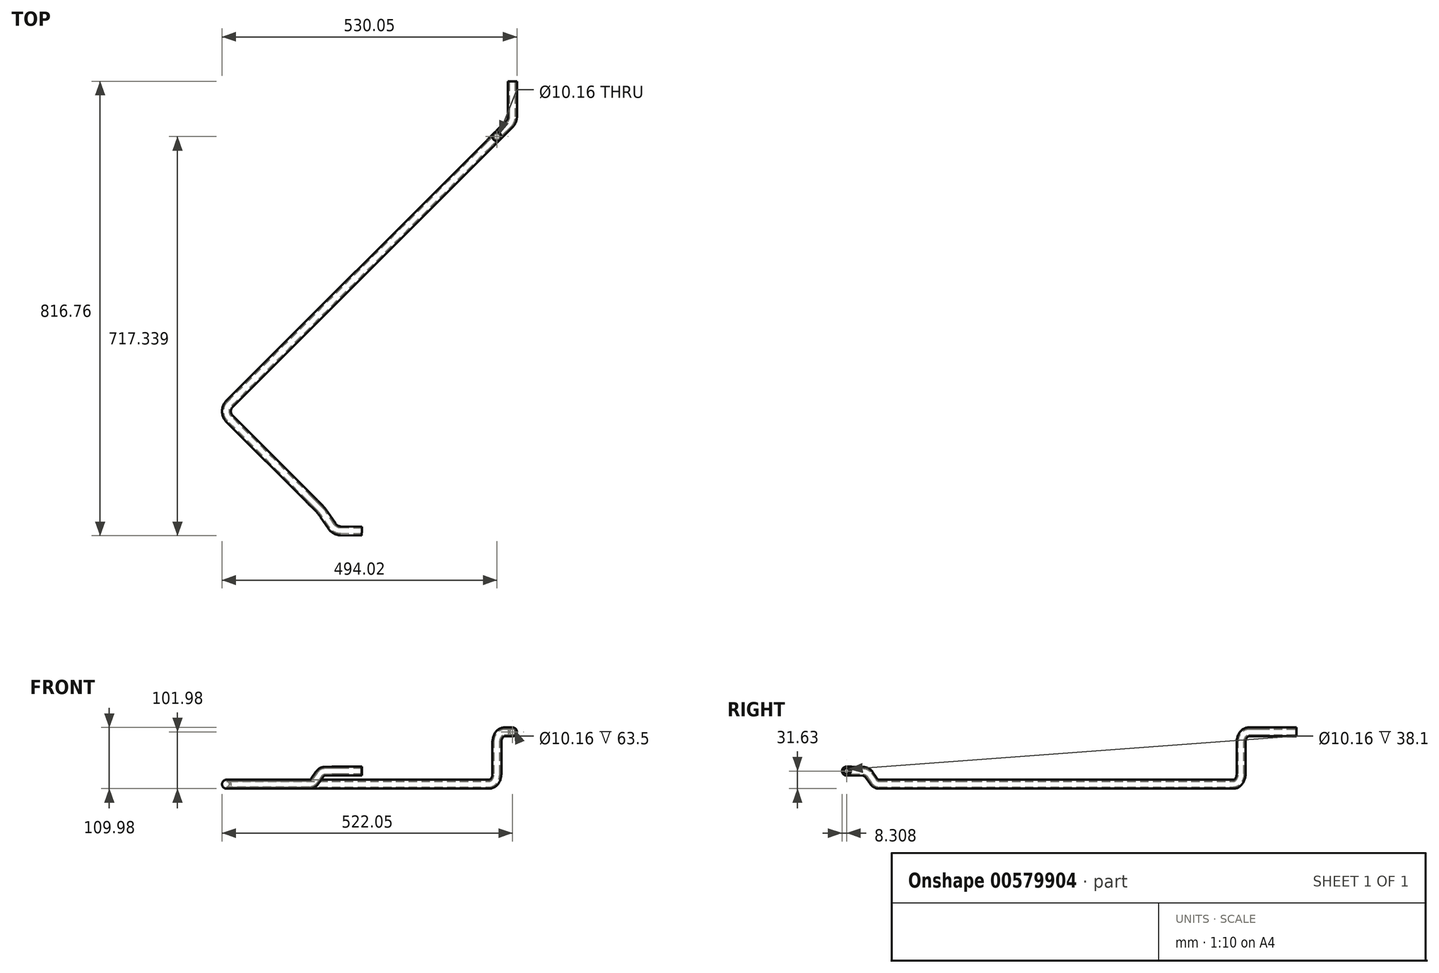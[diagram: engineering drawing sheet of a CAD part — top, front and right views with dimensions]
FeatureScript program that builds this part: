
annotation { "Feature Type Name" : "Feature", "Feature Type Description" : "" }
export const myFeature = defineFeature(function(context is Context, id is Id, definition is map)
    precondition{}
    {
        {
            var Q0;
            Q0=qCreatedBy(makeId("Front.planeOp"),FACE);
            var sketch = newSketch(context, id + "F0", { "sketchPlane" : qUnion([Q0])});
            skCircle(sketch, "E0", {"center": v(0, 0) * mm, "radius": 8 * mm});
            skCircle(sketch, "E1", {"center": v(0, 0) * mm, "radius": 5.08 * mm});
            skSolve(sketch);
        }
        {
            var Q0;
            Q0=qSketchRegion(id+"F0",true);
            extrude(context, id + "F1", {"entities" : qUnion([Q0]), "depth" : 63.5 * mm, "offsetDistance" : 25.4 * mm});
        }
        {
            var Q0;
            Q0=makeQuery(id+"F1.opExtrude","CAP_FACE",FACE,{"disambiguationData":[OSD([sQuery(id+"F0.wireOp",EDGE,"E0"),sQuery(id+"F0.wireOp",EDGE,"E1")])],"isStart":false});
            var sketch = newSketch(context, id + "F2", { "sketchPlane" : qUnion([Q0])});
            skCircle(sketch, "E2", {"center": v(0, 0) * mm, "radius": 5.08 * mm});
            skCircle(sketch, "E3", {"center": v(0, 0) * mm, "radius": 8 * mm});
            skLineSegment(sketch, "E4", {"start": v(-19.05, 9.37) * mm, "end": v(-19.05, -12.33) * mm});
            skSolve(sketch);
        }
        {
            var Q0;
            Q0 = qSketchRegion(id + "F2", true);
            var Q1;
            Q1=sQuery(id+"F2.wireOp",EDGE,"E4");
            revolve(context, id + "F3", {"operationType" : NewBodyOperationType.ADD, "entities" : qUnion([Q0]), "axis" : qUnion([Q1]), "revolveType" : RevolveType.ONE_DIRECTION, "angle" : 45 * degree});
        }
        {
            var Q0;
            Q0=makeQuery(id+"F3.opRevolve","CAP_FACE",FACE,{"disambiguationData":[OSD([sQuery(id+"F2.wireOp",EDGE,"E2"),sQuery(id+"F2.wireOp",EDGE,"E3")])],"isStart":false});
            var sketch = newSketch(context, id + "F4", { "sketchPlane" : qUnion([Q0])});
            skCircle(sketch, "E5", {"center": v(50.48, 0) * mm, "radius": 5.08 * mm});
            skCircle(sketch, "E6", {"center": v(50.48, 0) * mm, "radius": 8 * mm});
            skSolve(sketch);
        }
        {
            var Q0;
            Q0 = qSketchRegion(id + "F4", true);
            extrude(context, id + "F5", {"entities" : qUnion([Q0]), "operationType" : NewBodyOperationType.ADD, "depth" : 12.7 * mm, "offsetDistance" : 25.4 * mm});
        }
        {
            var Q0;
            Q0=makeQuery(id+"F5.opExtrude","CAP_FACE",FACE,{"disambiguationData":[OSD([sQuery(id+"F4.wireOp",EDGE,"E5"),sQuery(id+"F4.wireOp",EDGE,"E6")])],"isStart":false});
            var sketch = newSketch(context, id + "F6", { "sketchPlane" : qUnion([Q0])});
            skCircle(sketch, "E7", {"center": v(50.48, 0) * mm, "radius": 5.08 * mm});
            skCircle(sketch, "E8", {"center": v(50.48, 0) * mm, "radius": 8 * mm});
            skLineSegment(sketch, "E9", {"start": v(33.2, -19.05) * mm, "end": v(65.64, -19.05) * mm});
            skSolve(sketch);
        }
        {
            var Q0;
            Q0 = qSketchRegion(id + "F6", true);
            var Q1;
            Q1=sQuery(id+"F6.wireOp",EDGE,"E9");
            revolve(context, id + "F7", {"operationType" : NewBodyOperationType.ADD, "entities" : qUnion([Q0]), "axis" : qUnion([Q1]), "revolveType" : RevolveType.ONE_DIRECTION, "angle" : 90 * degree});
        }
        {
            var Q0;
            Q0=makeQuery(id+"F7.opRevolve","CAP_FACE",FACE,{"disambiguationData":[OSD([sQuery(id+"F6.wireOp",EDGE,"E7"),sQuery(id+"F6.wireOp",EDGE,"E8")])],"isStart":false});
            var sketch = newSketch(context, id + "F8", { "sketchPlane" : qUnion([Q0])});
            skCircle(sketch, "E10", {"center": v(-28.03, 99.42) * mm, "radius": 5.08 * mm});
            skCircle(sketch, "E11", {"center": v(-28.03, 99.42) * mm, "radius": 8 * mm});
            skSolve(sketch);
        }
        {
            var Q0;
            Q0 = qSketchRegion(id + "F8", true);
            extrude(context, id + "F9", {"entities" : qUnion([Q0]), "operationType" : NewBodyOperationType.ADD, "depth" : 55.88 * mm, "offsetDistance" : 25.4 * mm});
        }
        {
            var Q0;
            Q0=makeQuery(id+"F9.opExtrude","CAP_FACE",FACE,{"disambiguationData":[OSD([sQuery(id+"F8.wireOp",EDGE,"E10"),sQuery(id+"F8.wireOp",EDGE,"E11")])],"isStart":false});
            var sketch = newSketch(context, id + "F10", { "sketchPlane" : qUnion([Q0])});
            skCircle(sketch, "E12", {"center": v(-28.03, 99.42) * mm, "radius": 5.08 * mm});
            skCircle(sketch, "E13", {"center": v(-28.03, 99.42) * mm, "radius": 8 * mm});
            skLineSegment(sketch, "E14", {"start": v(-54.97, 99.42) * mm, "end": v(-28.03, 126.36) * mm});
            skSolve(sketch);
        }
        {
            var Q0;
            Q0 = qSketchRegion(id + "F10", true);
            var Q1;
            Q1=sQuery(id+"F10.wireOp",EDGE,"E14");
            revolve(context, id + "F11", {"operationType" : NewBodyOperationType.ADD, "entities" : qUnion([Q0]), "axis" : qUnion([Q1]), "revolveType" : RevolveType.ONE_DIRECTION, "oppositeDirection" : true, "angle" : 90 * degree});
        }
        {
            var Q0;
            Q0=makeQuery(id+"F11.opRevolve","CAP_FACE",FACE,{"disambiguationData":[OSD([sQuery(id+"F10.wireOp",EDGE,"E12"),sQuery(id+"F10.wireOp",EDGE,"E13")])],"isStart":false});
            var sketch = newSketch(context, id + "F12", { "sketchPlane" : qUnion([Q0])});
            skCircle(sketch, "E15", {"center": v(50.48, -93.98) * mm, "radius": 5.08 * mm});
            skCircle(sketch, "E16", {"center": v(50.48, -93.98) * mm, "radius": 8 * mm});
            skSolve(sketch);
        }
        {
            var Q0;
            Q0 = qSketchRegion(id + "F12", true);
            extrude(context, id + "F13", {"entities" : qUnion([Q0]), "operationType" : NewBodyOperationType.ADD, "depth" : 660.4 * mm, "offsetDistance" : 25.4 * mm});
        }
        {
            var Q0;
            Q0=makeQuery(id+"F13.opExtrude","CAP_FACE",FACE,{"disambiguationData":[OSD([sQuery(id+"F12.wireOp",EDGE,"E15"),sQuery(id+"F12.wireOp",EDGE,"E16")])],"isStart":false});
            var sketch = newSketch(context, id + "F14", { "sketchPlane" : qUnion([Q0])});
            skCircle(sketch, "E17", {"center": v(50.48, -93.98) * mm, "radius": 5.08 * mm});
            skCircle(sketch, "E18", {"center": v(50.48, -93.98) * mm, "radius": 8 * mm});
            skLineSegment(sketch, "E19", {"start": v(69.53, -87) * mm, "end": v(69.53, -100.05) * mm});
            skSolve(sketch);
        }
        {
            var Q0;
            Q0 = qSketchRegion(id + "F14", true);
            var Q1;
            Q1=sQuery(id+"F14.wireOp",EDGE,"E19");
            revolve(context, id + "F15", {"operationType" : NewBodyOperationType.ADD, "entities" : qUnion([Q0]), "axis" : qUnion([Q1]), "revolveType" : RevolveType.ONE_DIRECTION, "oppositeDirection" : true, "angle" : 90 * degree});
        }
        {
            var Q0;
            Q0=makeQuery(id+"F15.opRevolve","CAP_FACE",FACE,{"disambiguationData":[OSD([sQuery(id+"F14.wireOp",EDGE,"E17"),sQuery(id+"F14.wireOp",EDGE,"E18")])],"isStart":false});
            var sketch = newSketch(context, id + "F16", { "sketchPlane" : qUnion([Q0])});
            skCircle(sketch, "E20", {"center": v(-788.62, -93.98) * mm, "radius": 5.08 * mm});
            skCircle(sketch, "E21", {"center": v(-788.62, -93.98) * mm, "radius": 8 * mm});
            skSolve(sketch);
        }
        {
            var Q0;
            Q0 = qSketchRegion(id + "F16", true);
            extrude(context, id + "F17", {"entities" : qUnion([Q0]), "operationType" : NewBodyOperationType.ADD, "depth" : 203.2 * mm, "offsetDistance" : 25.4 * mm});
        }
        {
            var Q0;
            Q0=makeQuery(id+"F17.opExtrude","CAP_FACE",FACE,{"disambiguationData":[OSD([sQuery(id+"F16.wireOp",EDGE,"E20"),sQuery(id+"F16.wireOp",EDGE,"E21")])],"isStart":false});
            var sketch = newSketch(context, id + "F18", { "sketchPlane" : qUnion([Q0])});
            skCircle(sketch, "E22", {"center": v(-788.62, -93.98) * mm, "radius": 5.08 * mm});
            skCircle(sketch, "E23", {"center": v(-788.62, -93.98) * mm, "radius": 8 * mm});
            skLineSegment(sketch, "E24", {"start": v(-797.6, -74.93) * mm, "end": v(-780.75, -74.93) * mm});
            skSolve(sketch);
        }
        {
            var Q0;
            Q0 = qSketchRegion(id + "F18", true);
            var Q1;
            Q1=sQuery(id+"F18.wireOp",EDGE,"E24");
            revolve(context, id + "F19", {"operationType" : NewBodyOperationType.ADD, "entities" : qUnion([Q0]), "axis" : qUnion([Q1]), "revolveType" : RevolveType.ONE_DIRECTION, "oppositeDirection" : true, "angle" : 45 * degree});
        }
        {
            var Q0;
            Q0=makeQuery(id+"F19.opRevolve","CAP_FACE",FACE,{"disambiguationData":[OSD([sQuery(id+"F18.wireOp",EDGE,"E22"),sQuery(id+"F18.wireOp",EDGE,"E23")])],"isStart":false});
            var sketch = newSketch(context, id + "F20", { "sketchPlane" : qUnion([Q0])});
            skCircle(sketch, "E25", {"center": v(-490.98, -671.59) * mm, "radius": 5.08 * mm});
            skCircle(sketch, "E26", {"center": v(-490.98, -671.59) * mm, "radius": 8 * mm});
            skSolve(sketch);
        }
        {
            var Q0;
            Q0 = qSketchRegion(id + "F20", true);
            extrude(context, id + "F21", {"entities" : qUnion([Q0]), "operationType" : NewBodyOperationType.ADD, "depth" : 16.5 * mm, "offsetDistance" : 25.4 * mm});
        }
        {
            var Q0;
            Q0=makeQuery(id+"F21.opExtrude","CAP_FACE",FACE,{"disambiguationData":[OSD([sQuery(id+"F20.wireOp",EDGE,"E25"),sQuery(id+"F20.wireOp",EDGE,"E26")])],"isStart":false});
            var sketch = newSketch(context, id + "F22", { "sketchPlane" : qUnion([Q0])});
            skCircle(sketch, "E27", {"center": v(-490.98, -671.59) * mm, "radius": 5.08 * mm});
            skCircle(sketch, "E28", {"center": v(-490.98, -671.59) * mm, "radius": 8 * mm});
            skLineSegment(sketch, "E29", {"start": v(-493.52, -692.74) * mm, "end": v(-472.45, -685.18) * mm});
            skSolve(sketch);
        }
        {
            var Q0;
            Q0 = qSketchRegion(id + "F22", true);
            var Q1;
            Q1=sQuery(id+"F22.wireOp",EDGE,"E29");
            revolve(context, id + "F23", {"operationType" : NewBodyOperationType.ADD, "entities" : qUnion([Q0]), "axis" : qUnion([Q1]), "revolveType" : RevolveType.ONE_DIRECTION, "angle" : 45 * degree});
        }
        {
            var Q0;
            Q0=makeQuery(id+"F23.opRevolve","CAP_FACE",FACE,{"disambiguationData":[OSD([sQuery(id+"F22.wireOp",EDGE,"E27"),sQuery(id+"F22.wireOp",EDGE,"E28")])],"isStart":false});
            var sketch = newSketch(context, id + "F24", { "sketchPlane" : qUnion([Q0])});
            skCircle(sketch, "E30", {"center": v(-715.93, -88.12) * mm, "radius": 5.08 * mm});
            skCircle(sketch, "E31", {"center": v(-715.93, -88.12) * mm, "radius": 8 * mm});
            skSolve(sketch);
        }
        {
            var Q0;
            Q0 = qSketchRegion(id + "F24", true);
            extrude(context, id + "F25", {"entities" : qUnion([Q0]), "operationType" : NewBodyOperationType.ADD, "depth" : 25.4 * mm, "offsetDistance" : 25.4 * mm});
        }
        {
            var Q0;
            Q0=makeQuery(id+"F25.opExtrude","CAP_FACE",FACE,{"disambiguationData":[OSD([sQuery(id+"F24.wireOp",EDGE,"E30"),sQuery(id+"F24.wireOp",EDGE,"E31")])],"isStart":false});
            var sketch = newSketch(context, id + "F26", { "sketchPlane" : qUnion([Q0])});
            skCircle(sketch, "E32", {"center": v(-715.93, -88.12) * mm, "radius": 5.08 * mm});
            skCircle(sketch, "E33", {"center": v(-715.93, -88.12) * mm, "radius": 8 * mm});
            skLineSegment(sketch, "E34", {"start": v(-696.88, -79.28) * mm, "end": v(-696.88, -95.32) * mm});
            skSolve(sketch);
        }
        {
            var Q0;
            Q0 = qSketchRegion(id + "F26", true);
            var Q1;
            Q1=sQuery(id+"F26.wireOp",EDGE,"E34");
            revolve(context, id + "F27", {"operationType" : NewBodyOperationType.ADD, "entities" : qUnion([Q0]), "axis" : qUnion([Q1]), "revolveType" : RevolveType.ONE_DIRECTION, "oppositeDirection" : true, "angle" : 55 * degree});
        }
        {
            var Q0;
            Q0=makeQuery(id+"F27.opRevolve","CAP_FACE",FACE,{"disambiguationData":[OSD([sQuery(id+"F26.wireOp",EDGE,"E32"),sQuery(id+"F26.wireOp",EDGE,"E33")])],"isStart":false});
            var sketch = newSketch(context, id + "F28", { "sketchPlane" : qUnion([Q0])});
            skCircle(sketch, "E35", {"center": v(-812.97, -70.25) * mm, "radius": 5.08 * mm});
            skCircle(sketch, "E36", {"center": v(-812.97, -70.25) * mm, "radius": 8 * mm});
            skSolve(sketch);
        }
        {
            var Q0;
            Q0 = qSketchRegion(id + "F28", true);
            extrude(context, id + "F29", {"entities" : qUnion([Q0]), "operationType" : NewBodyOperationType.ADD, "depth" : 38.1 * mm, "offsetDistance" : 25.4 * mm});
        }
    });
